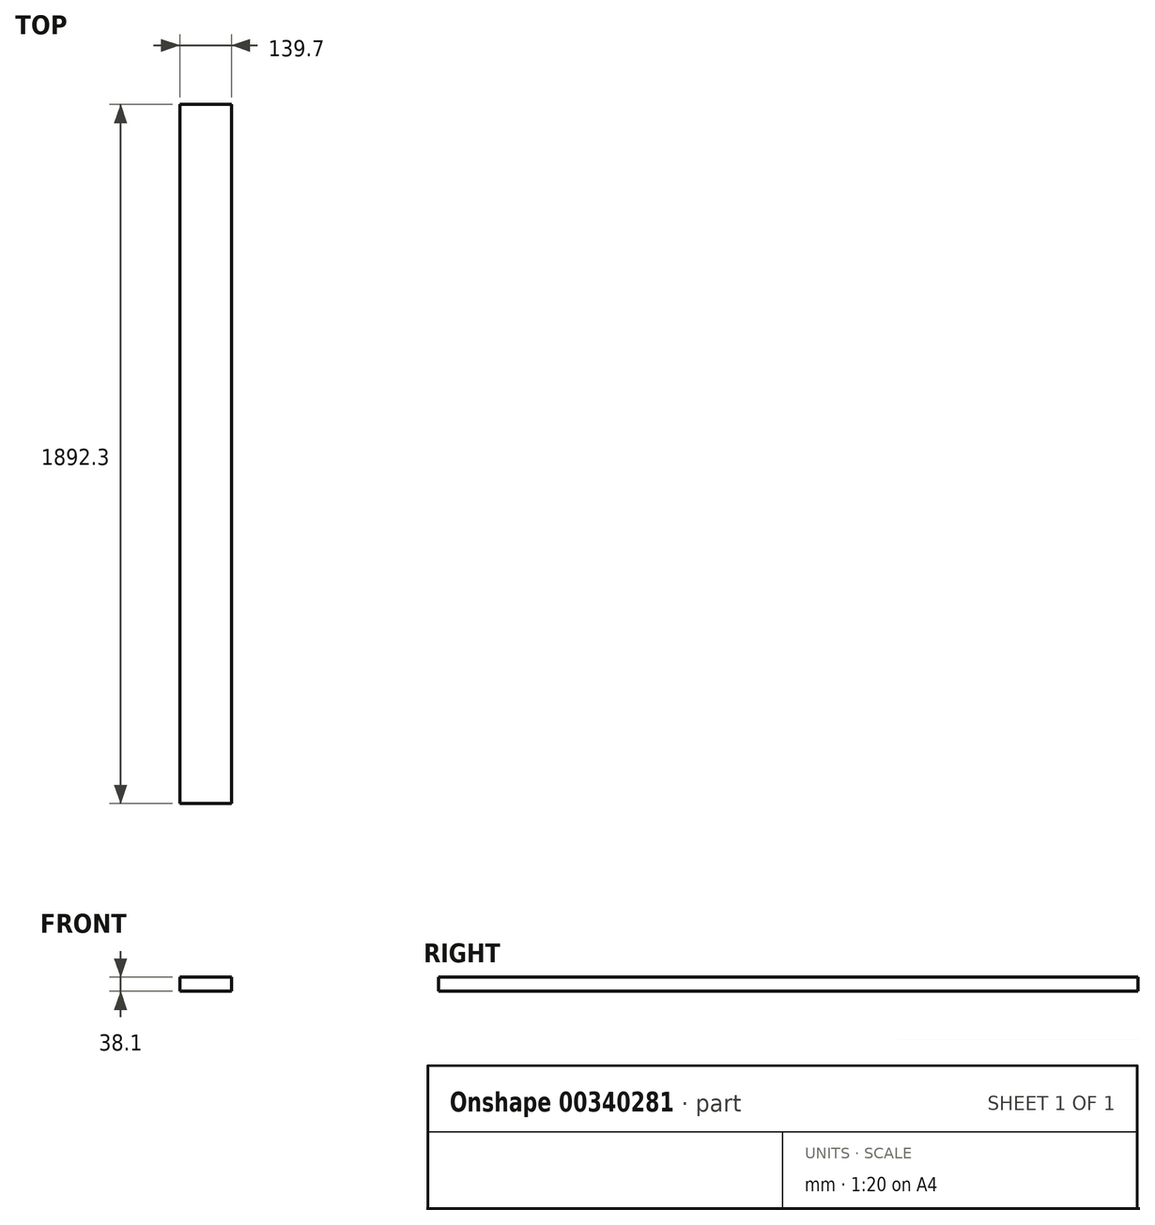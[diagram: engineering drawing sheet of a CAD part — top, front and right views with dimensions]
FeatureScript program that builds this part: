
annotation { "Feature Type Name" : "Feature", "Feature Type Description" : "" }
export const myFeature = defineFeature(function(context is Context, id is Id, definition is map)
    precondition{}
    {
        {
            var Q0;
            Q0=qCreatedBy(makeId("Front.planeOp"),FACE);
            var sketch = newSketch(context, id + "F0", { "sketchPlane" : qUnion([Q0])});
            skLineSegment(sketch, "E0.bottom", {"start": v(69.85, -19.05) * mm, "end": v(-69.85, -19.05) * mm});
            skLineSegment(sketch, "E0.top", {"start": v(69.85, 19.05) * mm, "end": v(-69.85, 19.05) * mm});
            skLineSegment(sketch, "E0.left", {"start": v(69.85, -19.05) * mm, "end": v(69.85, 19.05) * mm});
            skLineSegment(sketch, "E0.right", {"start": v(-69.85, -19.05) * mm, "end": v(-69.85, 19.05) * mm});
            skPoint(sketch, "E0.middle", {"position": v(0, 0) * mm});
            skSolve(sketch);
        }
        {
            var Q0;
            Q0 = qSketchRegion(id + "F0", true);
            extrude(context, id + "F1", {"entities" : qUnion([Q0]), "endBound" : BoundingType.SYMMETRIC, "depth" : 1892.3 * mm});
        }
    });
